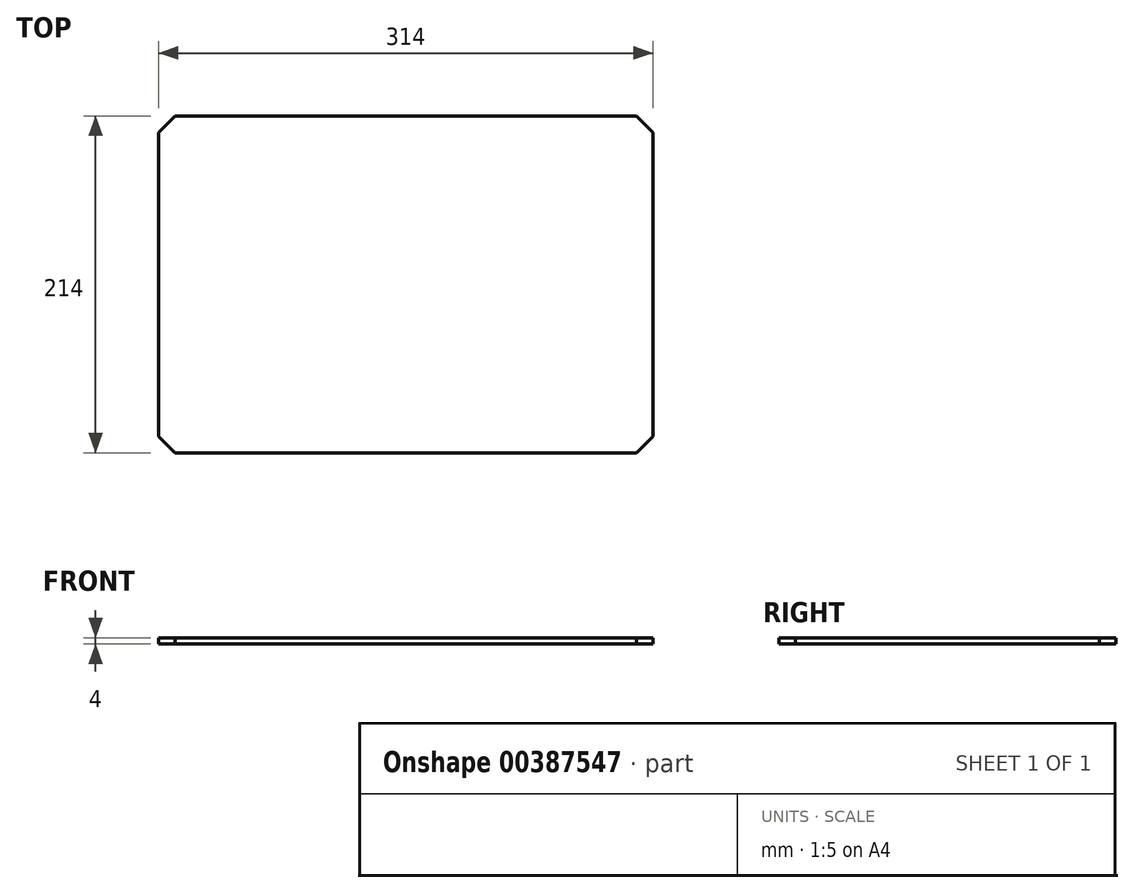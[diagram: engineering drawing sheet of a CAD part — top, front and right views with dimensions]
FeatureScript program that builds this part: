
annotation { "Feature Type Name" : "Feature", "Feature Type Description" : "" }
export const myFeature = defineFeature(function(context is Context, id is Id, definition is map)
    precondition{}
    {
        {
            var Q0;
            Q0=qCreatedBy(makeId("Top.planeOp"),FACE);
            var sketch = newSketch(context, id + "F0", { "sketchPlane" : qUnion([Q0])});
            skLineSegment(sketch, "E0.bottom", {"start": v(157, 107) * mm, "end": v(-157, 107) * mm});
            skLineSegment(sketch, "E0.top", {"start": v(157, -107) * mm, "end": v(-157, -107) * mm});
            skLineSegment(sketch, "E0.left", {"start": v(157, 107) * mm, "end": v(157, -107) * mm});
            skLineSegment(sketch, "E0.right", {"start": v(-157, 107) * mm, "end": v(-157, -107) * mm});
            skPoint(sketch, "E0.middle", {"position": v(0, 0) * mm});
            skSolve(sketch);
        }
        {
            var Q0;
            Q0=qSketchRegion(id+"F0",true);
            extrude(context, id + "F1", {"entities" : qUnion([Q0]), "depth" : 4 * mm});
        }
        {
            var Q0;
            Q0=makeQuery(id+"F1.opExtrude","SWEPT_EDGE",EDGE,{"disambiguationData":[OSD([sQuery(id+"F0.wireOp",EDGE,"E0.top"),sQuery(id+"F0.wireOp",EDGE,"E0.right")])]});
            var Q1;
            Q1=makeQuery(id+"F1.opExtrude","SWEPT_EDGE",EDGE,{"disambiguationData":[OSD([sQuery(id+"F0.wireOp",EDGE,"E0.top"),sQuery(id+"F0.wireOp",EDGE,"E0.left")])]});
            var Q2;
            Q2=makeQuery(id+"F1.opExtrude","SWEPT_EDGE",EDGE,{"disambiguationData":[OSD([sQuery(id+"F0.wireOp",EDGE,"E0.bottom"),sQuery(id+"F0.wireOp",EDGE,"E0.left")])]});
            var Q3;
            Q3=makeQuery(id+"F1.opExtrude","SWEPT_EDGE",EDGE,{"disambiguationData":[OSD([sQuery(id+"F0.wireOp",EDGE,"E0.bottom"),sQuery(id+"F0.wireOp",EDGE,"E0.right")])]});
            chamfer(context, id + "F2", {"entities" : qUnion([Q0, Q1, Q2, Q3]), "width" : 10.5 * mm, "tangentPropagation" : true});
        }
    });
